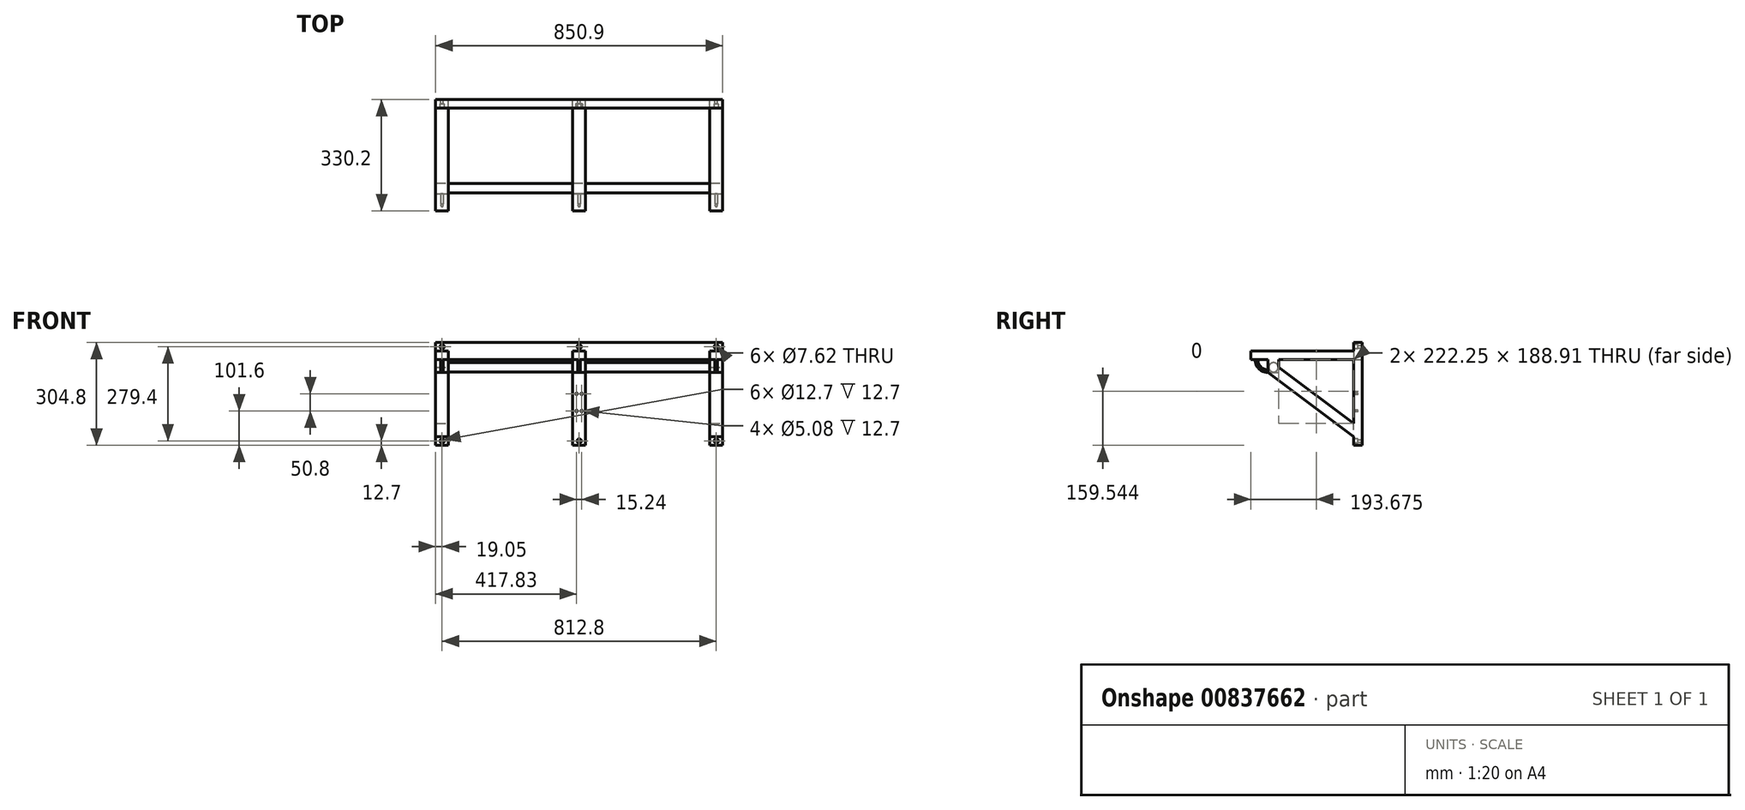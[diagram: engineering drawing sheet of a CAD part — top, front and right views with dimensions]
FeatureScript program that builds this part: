
annotation { "Feature Type Name" : "Feature", "Feature Type Description" : "" }
export const myFeature = defineFeature(function(context is Context, id is Id, definition is map)
    precondition{}
    {
        {
            var Q0;
            Q0=qCreatedBy(makeId("Front.planeOp"),FACE);
            var sketch = newSketch(context, id + "F0", { "sketchPlane" : qUnion([Q0])});
            skLineSegment(sketch, "E0.bottom", {"start": v(19.05, -152.4) * mm, "end": v(-19.05, -152.4) * mm});
            skLineSegment(sketch, "E0.top", {"start": v(19.05, 152.4) * mm, "end": v(-19.05, 152.4) * mm});
            skLineSegment(sketch, "E0.left", {"start": v(19.05, -152.4) * mm, "end": v(19.05, 152.4) * mm});
            skLineSegment(sketch, "E0.right", {"start": v(-19.05, -152.4) * mm, "end": v(-19.05, 152.4) * mm});
            skPoint(sketch, "E0.middle", {"position": v(0, 0) * mm});
            skLineSegment(sketch, "E1.bottom", {"start": v(-387.35, -152.4) * mm, "end": v(-425.45, -152.4) * mm});
            skLineSegment(sketch, "E1.top", {"start": v(-387.35, 152.4) * mm, "end": v(-425.45, 152.4) * mm});
            skLineSegment(sketch, "E1.left", {"start": v(-387.35, -152.4) * mm, "end": v(-387.35, 152.4) * mm});
            skLineSegment(sketch, "E1.right", {"start": v(-425.45, -152.4) * mm, "end": v(-425.45, 152.4) * mm});
            skPoint(sketch, "E1.middle", {"position": v(-406.4, 0) * mm});
            skLineSegment(sketch, "E2.bottom", {"start": v(425.45, -152.4) * mm, "end": v(387.35, -152.4) * mm});
            skLineSegment(sketch, "E2.top", {"start": v(425.45, 152.4) * mm, "end": v(387.35, 152.4) * mm});
            skLineSegment(sketch, "E2.left", {"start": v(425.45, -152.4) * mm, "end": v(425.45, 152.4) * mm});
            skLineSegment(sketch, "E2.right", {"start": v(387.35, -152.4) * mm, "end": v(387.35, 152.4) * mm});
            skPoint(sketch, "E2.middle", {"position": v(406.4, 0) * mm});
            skLineSegment(sketch, "E3.bottom", {"start": v(425.45, 101.6) * mm, "end": v(-425.45, 101.6) * mm});
            skLineSegment(sketch, "E3.top", {"start": v(425.45, 127) * mm, "end": v(-425.45, 127) * mm});
            skLineSegment(sketch, "E3.left", {"start": v(425.45, 101.6) * mm, "end": v(425.45, 127) * mm});
            skLineSegment(sketch, "E3.right", {"start": v(-425.45, 101.6) * mm, "end": v(-425.45, 127) * mm});
            skPoint(sketch, "E3.middle", {"position": v(0, 114.3) * mm});
            skSolve(sketch);
        }
        {
            var Q0;
            Q0=qSketchRegion(id+"F0",true);
            extrude(context, id + "F1", {"entities" : qUnion([Q0]), "depth" : 25.4 * mm, "offsetDistance" : 25.4 * mm});
        }
        {
            var Q0;
            Q0=makeQuery(id+"F1.opExtrude","CAP_FACE",FACE,{"disambiguationData":[OSD([sQuery(id+"F0.wireOp",EDGE,"E0.bottom"),sQuery(id+"F0.wireOp",EDGE,"E0.top"),sQuery(id+"F0.wireOp",EDGE,"E0.left"),sQuery(id+"F0.wireOp",EDGE,"E0.right"),sQuery(id+"F0.wireOp",EDGE,"E1.bottom"),sQuery(id+"F0.wireOp",EDGE,"E1.top"),sQuery(id+"F0.wireOp",EDGE,"E1.left"),sQuery(id+"F0.wireOp",EDGE,"E1.right"),sQuery(id+"F0.wireOp",EDGE,"E2.bottom"),sQuery(id+"F0.wireOp",EDGE,"E2.top"),sQuery(id+"F0.wireOp",EDGE,"E2.left"),sQuery(id+"F0.wireOp",EDGE,"E2.right"),sQuery(id+"F0.wireOp",EDGE,"E3.bottom"),sQuery(id+"F0.wireOp",EDGE,"E3.top"),sQuery(id+"F0.wireOp",EDGE,"E3.left"),sQuery(id+"F0.wireOp",EDGE,"E3.right")])],"isStart":false});
            var sketch = newSketch(context, id + "F2", { "sketchPlane" : qUnion([Q0])});
            skLineSegment(sketch, "E4.bottom", {"start": v(-387.35, 101.6) * mm, "end": v(-425.45, 101.6) * mm});
            skLineSegment(sketch, "E4.top", {"start": v(-387.35, 127) * mm, "end": v(-425.45, 127) * mm});
            skLineSegment(sketch, "E4.left", {"start": v(-387.35, 101.6) * mm, "end": v(-387.35, 127) * mm});
            skLineSegment(sketch, "E4.right", {"start": v(-425.45, 101.6) * mm, "end": v(-425.45, 127) * mm});
            skLineSegment(sketch, "E5.bottom", {"start": v(-19.05, 127) * mm, "end": v(19.05, 127) * mm});
            skLineSegment(sketch, "E5.top", {"start": v(-19.05, 101.6) * mm, "end": v(19.05, 101.6) * mm});
            skLineSegment(sketch, "E5.left", {"start": v(-19.05, 127) * mm, "end": v(-19.05, 101.6) * mm});
            skLineSegment(sketch, "E5.right", {"start": v(19.05, 127) * mm, "end": v(19.05, 101.6) * mm});
            skLineSegment(sketch, "E6.bottom", {"start": v(387.35, 127) * mm, "end": v(425.45, 127) * mm});
            skLineSegment(sketch, "E6.top", {"start": v(387.35, 101.6) * mm, "end": v(425.45, 101.6) * mm});
            skLineSegment(sketch, "E6.left", {"start": v(387.35, 127) * mm, "end": v(387.35, 101.6) * mm});
            skLineSegment(sketch, "E6.right", {"start": v(425.45, 127) * mm, "end": v(425.45, 101.6) * mm});
            skSolve(sketch);
        }
        {
            var Q0;
            Q0=qSketchRegion(id+"F2",true);
            extrude(context, id + "F3", {"entities" : qUnion([Q0]), "operationType" : NewBodyOperationType.ADD, "depth" : 304.8 * mm, "offsetDistance" : 25.4 * mm});
        }
        {
            var Q0;
            {var subQ0=sQuery(id+"F0.wireOp",EDGE,"E1.left");var subQ1=sQuery(id+"F0.wireOp",EDGE,"E1.top");var subQ2=sQuery(id+"F0.wireOp",EDGE,"E3.top");var subQ4=sQuery(id+"F0.wireOp",EDGE,"E3.right");var subQ5=sQuery(id+"F0.wireOp",EDGE,"E1.right");var subQ6=sQuery(id+"F0.wireOp",EDGE,"E0.right");var subQ7=makeQuery(id+"F1.opExtrude","CAP_FACE",FACE,{"disambiguationData":[OSD([sQuery(id+"F0.wireOp",EDGE,"E0.bottom"),sQuery(id+"F0.wireOp",EDGE,"E0.top"),sQuery(id+"F0.wireOp",EDGE,"E0.left"),subQ6,sQuery(id+"F0.wireOp",EDGE,"E1.bottom"),subQ1,subQ0,subQ5,sQuery(id+"F0.wireOp",EDGE,"E2.bottom"),sQuery(id+"F0.wireOp",EDGE,"E2.top"),sQuery(id+"F0.wireOp",EDGE,"E2.left"),sQuery(id+"F0.wireOp",EDGE,"E2.right"),sQuery(id+"F0.wireOp",EDGE,"E3.bottom"),subQ2,sQuery(id+"F0.wireOp",EDGE,"E3.left"),subQ4])],"isStart":false});Q0=makeQuery(id+"F3.boolean.opBoolean","SPLIT",FACE,{"disambiguationData":[TD([subQ7,makeQuery(id+"F1.opExtrude","SWEPT_FACE",FACE,{"disambiguationData":[OSD([subQ1])]}),makeQuery(id+"F1.opExtrude","SWEPT_FACE",FACE,{"disambiguationData":[OSD([subQ0]),TDD([makeQuery(id+"F0.imprint","IMPRINT",EDGE,{"disambiguationData":[TD([[makeQuery(id+"F0.imprint","INTERSECT",VERTEX,{"derivedFrom":[subQ1,subQ0]}),1.0]])],"derivedFrom":subQ0})])]}),makeQuery(id+"F1.opExtrude","SWEPT_FACE",FACE,{"disambiguationData":[OSD([subQ5,subQ4])]}),makeQuery(id+"F1.opExtrude","SWEPT_FACE",FACE,{"disambiguationData":[OSD([subQ2]),TDD([makeQuery(id+"F0.imprint","IMPRINT",EDGE,{"disambiguationData":[TD([[makeQuery(id+"F0.imprint","INTERSECT",VERTEX,{"derivedFrom":[subQ6,subQ2]}),-1.0]])],"derivedFrom":subQ2})])]}),makeQuery(id+"F3.opExtrude","SWEPT_FACE",FACE,{"disambiguationData":[OSD([sQuery(id+"F2.wireOp",EDGE,"E4.top")])]}),makeQuery(id+"F3.opExtrude","SWEPT_FACE",FACE,{"disambiguationData":[OSD([sQuery(id+"F2.wireOp",EDGE,"E4.left")])]}),makeQuery(id+"F3.opExtrude","SWEPT_FACE",FACE,{"disambiguationData":[OSD([sQuery(id+"F2.wireOp",EDGE,"E4.right")])]})])],"derivedFrom":subQ7});}
            var sketch = newSketch(context, id + "F4", { "sketchPlane" : qUnion([Q0])});
            skLineSegment(sketch, "E7.bottom", {"start": v(-425.45, 152.4) * mm, "end": v(425.45, 152.4) * mm});
            skLineSegment(sketch, "E7.top", {"start": v(-425.45, 127) * mm, "end": v(425.45, 127) * mm});
            skLineSegment(sketch, "E7.left", {"start": v(-425.45, 152.4) * mm, "end": v(-425.45, 127) * mm});
            skLineSegment(sketch, "E7.right", {"start": v(425.45, 152.4) * mm, "end": v(425.45, 127) * mm});
            skSolve(sketch);
        }
        {
            var Q0;
            Q0 = qSketchRegion(id + "F4", true);
            extrude(context, id + "F5", {"entities" : qUnion([Q0]), "operationType" : NewBodyOperationType.ADD, "oppositeDirection" : true, "depth" : 25.4 * mm, "offsetDistance" : 25.4 * mm});
        }
        {
            var Q0;
            Q0=makeQuery(id+"F3.boolean.opBoolean","MERGE",FACE,{"derivedFrom":[makeQuery(id+"F1.opExtrude","SWEPT_FACE",FACE,{"disambiguationData":[OSD([sQuery(id+"F0.wireOp",EDGE,"E2.left"),sQuery(id+"F0.wireOp",EDGE,"E3.left")])]}),makeQuery(id+"F3.opExtrude","SWEPT_FACE",FACE,{"disambiguationData":[OSD([sQuery(id+"F2.wireOp",EDGE,"E6.right")])]})]});
            var sketch = newSketch(context, id + "F6", { "sketchPlane" : qUnion([Q0])});
            skLineSegment(sketch, "E8", {"start": v(-25.4, -127) * mm, "end": v(-279.4, 63.5) * mm});
            skLineSegment(sketch, "E9", {"start": v(-279.4, 63.5) * mm, "end": v(-279.4, 101.6) * mm});
            skLineSegment(sketch, "E10", {"start": v(-279.4, 101.6) * mm, "end": v(-247.65, 101.6) * mm});
            skLineSegment(sketch, "E11", {"start": v(-247.65, 101.6) * mm, "end": v(-247.65, 79.38) * mm});
            skLineSegment(sketch, "E12", {"start": v(-247.65, 79.38) * mm, "end": v(-25.4, -87.31) * mm});
            skLineSegment(sketch, "E13", {"start": v(-25.4, -87.31) * mm, "end": v(-25.4, -127) * mm});
            skSolve(sketch);
        }
        {
            var Q0;
            Q0 = qSketchRegion(id + "F6", true);
            extrude(context, id + "F7", {"entities" : qUnion([Q0]), "operationType" : NewBodyOperationType.ADD, "oppositeDirection" : true, "depth" : 38.1 * mm, "offsetDistance" : 25.4 * mm});
        }
        {
            var Q0;
            Q0=makeQuery(id+"F3.opExtrude","SWEPT_FACE",FACE,{"disambiguationData":[OSD([sQuery(id+"F2.wireOp",EDGE,"E4.left")])]});
            var sketch = newSketch(context, id + "F8", { "sketchPlane" : qUnion([Q0])});
            skLineSegment(sketch, "E14", {"start": v(-25.4, -127) * mm, "end": v(-279.4, 63.5) * mm});
            skLineSegment(sketch, "E15", {"start": v(-279.4, 63.5) * mm, "end": v(-279.4, 101.6) * mm});
            skLineSegment(sketch, "E16", {"start": v(-279.4, 101.6) * mm, "end": v(-247.65, 101.6) * mm});
            skLineSegment(sketch, "E17", {"start": v(-247.65, 101.6) * mm, "end": v(-247.65, 79.38) * mm});
            skLineSegment(sketch, "E18", {"start": v(-247.65, 79.38) * mm, "end": v(-25.4, -87.31) * mm});
            skLineSegment(sketch, "E19", {"start": v(-25.4, -87.31) * mm, "end": v(-25.4, -127) * mm});
            skSolve(sketch);
        }
        {
            var Q0;
            Q0 = qSketchRegion(id + "F8", true);
            extrude(context, id + "F9", {"entities" : qUnion([Q0]), "operationType" : NewBodyOperationType.ADD, "oppositeDirection" : true, "depth" : 38.1 * mm, "offsetDistance" : 25.4 * mm});
        }
        {
            var Q0;
            Q0=makeQuery(id+"F3.opExtrude","SWEPT_FACE",FACE,{"disambiguationData":[OSD([sQuery(id+"F2.wireOp",EDGE,"E5.right")])]});
            var sketch = newSketch(context, id + "F10", { "sketchPlane" : qUnion([Q0])});
            skLineSegment(sketch, "E20.bottom", {"start": v(-279.7, 101.6) * mm, "end": v(-247.95, 101.6) * mm});
            skLineSegment(sketch, "E20.top", {"start": v(-279.7, 63.5) * mm, "end": v(-247.95, 63.5) * mm});
            skLineSegment(sketch, "E20.left", {"start": v(-279.7, 101.6) * mm, "end": v(-279.7, 63.5) * mm});
            skLineSegment(sketch, "E20.right", {"start": v(-247.95, 101.6) * mm, "end": v(-247.95, 63.5) * mm});
            skSolve(sketch);
        }
        {
            var Q0;
            Q0 = qSketchRegion(id + "F10", true);
            extrude(context, id + "F11", {"entities" : qUnion([Q0]), "operationType" : NewBodyOperationType.ADD, "oppositeDirection" : true, "depth" : 38.1 * mm, "offsetDistance" : 25.4 * mm});
        }
        {
            var Q0;
            {var subQ0=sQuery(id+"F0.wireOp",EDGE,"E0.right");var subQ1=sQuery(id+"F0.wireOp",EDGE,"E0.bottom");var subQ2=sQuery(id+"F0.wireOp",EDGE,"E3.bottom");var subQ3=makeQuery(id+"F0.imprint","INTERSECT",VERTEX,{"derivedFrom":[subQ0,subQ2]});var subQ4=sQuery(id+"F0.wireOp",EDGE,"E0.left");var subQ5=makeQuery(id+"F0.imprint","INTERSECT",VERTEX,{"derivedFrom":[subQ4,subQ2]});var subQ6=sQuery(id+"F0.wireOp",EDGE,"E2.right");var subQ7=sQuery(id+"F0.wireOp",EDGE,"E1.left");var subQ8=makeQuery(id+"F1.opExtrude","CAP_FACE",FACE,{"disambiguationData":[OSD([subQ1,sQuery(id+"F0.wireOp",EDGE,"E0.top"),subQ4,subQ0,sQuery(id+"F0.wireOp",EDGE,"E1.bottom"),sQuery(id+"F0.wireOp",EDGE,"E1.top"),subQ7,sQuery(id+"F0.wireOp",EDGE,"E1.right"),sQuery(id+"F0.wireOp",EDGE,"E2.bottom"),sQuery(id+"F0.wireOp",EDGE,"E2.top"),sQuery(id+"F0.wireOp",EDGE,"E2.left"),subQ6,subQ2,sQuery(id+"F0.wireOp",EDGE,"E3.top"),sQuery(id+"F0.wireOp",EDGE,"E3.left"),sQuery(id+"F0.wireOp",EDGE,"E3.right")])],"isStart":false});Q0=makeQuery(id+"F3.boolean.opBoolean","SPLIT",FACE,{"disambiguationData":[TD([makeQuery(id+"F1.opExtrude","SWEPT_FACE",FACE,{"disambiguationData":[OSD([subQ1])]}),subQ8,makeQuery(id+"F1.opExtrude","SWEPT_FACE",FACE,{"disambiguationData":[OSD([subQ4]),TDD([makeQuery(id+"F0.imprint","IMPRINT",EDGE,{"disambiguationData":[TD([[makeQuery(id+"F0.imprint","INTERSECT",VERTEX,{"derivedFrom":[subQ1,subQ4]}),-1.0]])],"derivedFrom":subQ4})])]}),makeQuery(id+"F1.opExtrude","SWEPT_FACE",FACE,{"disambiguationData":[OSD([subQ0]),TDD([makeQuery(id+"F0.imprint","IMPRINT",EDGE,{"disambiguationData":[TD([[makeQuery(id+"F0.imprint","INTERSECT",VERTEX,{"derivedFrom":[subQ1,subQ0]}),-1.0]])],"derivedFrom":subQ0})])]}),makeQuery(id+"F1.opExtrude","SWEPT_FACE",FACE,{"disambiguationData":[OSD([subQ2]),TDD([makeQuery(id+"F0.imprint","IMPRINT",EDGE,{"disambiguationData":[TD([[subQ5,1.0]])],"derivedFrom":subQ2})])]}),makeQuery(id+"F1.opExtrude","SWEPT_FACE",FACE,{"disambiguationData":[OSD([subQ2]),TDD([makeQuery(id+"F0.imprint","IMPRINT",EDGE,{"disambiguationData":[TD([[subQ3,-1.0]])],"derivedFrom":subQ2})])]}),makeQuery(id+"F3.opExtrude","SWEPT_FACE",FACE,{"disambiguationData":[OSD([sQuery(id+"F2.wireOp",EDGE,"E5.top")])]}),makeQuery(id+"F3.opExtrude","SWEPT_FACE",FACE,{"disambiguationData":[OSD([sQuery(id+"F2.wireOp",EDGE,"E5.left")])]}),makeQuery(id+"F3.opExtrude","SWEPT_FACE",FACE,{"disambiguationData":[OSD([sQuery(id+"F2.wireOp",EDGE,"E5.right")])]})])],"derivedFrom":subQ8});}
            var sketch = newSketch(context, id + "F12", { "sketchPlane" : qUnion([Q0])});
            skCircle(sketch, "E21", {"center": v(-7.62, 0) * mm, "radius": 2.54 * mm});
            skCircle(sketch, "E22.MirrorC", {"center": v(7.62, 0) * mm, "radius": 2.54 * mm});
            skCircle(sketch, "E23.MirrorC", {"center": v(-7.62, -50.8) * mm, "radius": 2.54 * mm});
            skCircle(sketch, "E24.MirrorC", {"center": v(7.62, -50.8) * mm, "radius": 2.54 * mm});
            skSolve(sketch);
        }
        {
            var Q0;
            Q0 = qSketchRegion(id + "F12", true);
            extrude(context, id + "F13", {"entities" : qUnion([Q0]), "operationType" : NewBodyOperationType.REMOVE, "oppositeDirection" : true, "depth" : 12.7 * mm, "offsetDistance" : 25.4 * mm});
        }
        {
            var Q0;
            Q0=qCreatedBy(makeId("Right.planeOp"),FACE);
            var sketch = newSketch(context, id + "F14", { "sketchPlane" : qUnion([Q0])});
            skCircle(sketch, "E25", {"center": v(-263.27, 78.74) * mm, "radius": 13.97 * mm});
            skSolve(sketch);
        }
        {
            var Q0;
            Q0 = qSketchRegion(id + "F14", true);
            extrude(context, id + "F15", {"entities" : qUnion([Q0]), "operationType" : NewBodyOperationType.ADD, "oppositeDirection" : true, "depth" : 406.4 * mm, "offsetDistance" : 25.4 * mm, "hasSecondDirection" : true, "secondDirectionOppositeDirection" : false, "secondDirectionDepth" : 406.4 * mm});
        }
        {
            var Q0;
            Q0=makeQuery(id+"F9.boolean.opBoolean","MERGE",FACE,{"derivedFrom":[makeQuery(id+"F3.boolean.opBoolean","MERGE",FACE,{"derivedFrom":[makeQuery(id+"F1.opExtrude","SWEPT_FACE",FACE,{"disambiguationData":[OSD([sQuery(id+"F0.wireOp",EDGE,"E1.right"),sQuery(id+"F0.wireOp",EDGE,"E3.right")])]}),makeQuery(id+"F3.opExtrude","SWEPT_FACE",FACE,{"disambiguationData":[OSD([sQuery(id+"F2.wireOp",EDGE,"E4.right")])]})]}),makeQuery(id+"F9.opExtrude","CAP_FACE",FACE,{"disambiguationData":[OSD([sQuery(id+"F8.wireOp",EDGE,"E14"),sQuery(id+"F8.wireOp",EDGE,"E15"),sQuery(id+"F8.wireOp",EDGE,"E16"),sQuery(id+"F8.wireOp",EDGE,"E17"),sQuery(id+"F8.wireOp",EDGE,"E18"),sQuery(id+"F8.wireOp",EDGE,"E19")])],"isStart":false})]});
            var sketch = newSketch(context, id + "F16", { "sketchPlane" : qUnion([Q0])});
            skArc(sketch, "E26", {"start": v(279.4, 63.5) * mm, "mid": v(306.34, 74.66) * mm, "end": v(317.5, 101.6) * mm});
            skArc(sketch, "E27", {"start": v(279.4, 71.12) * mm, "mid": v(300.95, 80.05) * mm, "end": v(309.88, 101.6) * mm});
            skLineSegment(sketch, "E28", {"start": v(309.88, 101.6) * mm, "end": v(317.5, 101.6) * mm});
            skLineSegment(sketch, "E29", {"start": v(279.4, 63.5) * mm, "end": v(279.4, 71.12) * mm});
            skSolve(sketch);
        }
        {
            var Q0;
            Q0 = qSketchRegion(id + "F16", true);
            extrude(context, id + "F17", {"entities" : qUnion([Q0]), "operationType" : NewBodyOperationType.ADD, "oppositeDirection" : true, "depth" : 38.1 * mm, "offsetDistance" : 25.4 * mm});
        }
        {
            var Q0;
            Q0=makeQuery(id+"F11.boolean.opBoolean","MERGE",FACE,{"derivedFrom":[makeQuery(id+"F3.opExtrude","SWEPT_FACE",FACE,{"disambiguationData":[OSD([sQuery(id+"F2.wireOp",EDGE,"E5.left")])]}),makeQuery(id+"F11.opExtrude","CAP_FACE",FACE,{"disambiguationData":[OSD([sQuery(id+"F10.wireOp",EDGE,"E20.bottom"),sQuery(id+"F10.wireOp",EDGE,"E20.top"),sQuery(id+"F10.wireOp",EDGE,"E20.left"),sQuery(id+"F10.wireOp",EDGE,"E20.right")])],"isStart":false})]});
            var sketch = newSketch(context, id + "F18", { "sketchPlane" : qUnion([Q0])});
            skArc(sketch, "E30", {"start": v(279.7, 63.5) * mm, "mid": v(306.64, 74.66) * mm, "end": v(317.8, 101.6) * mm});
            skArc(sketch, "E31", {"start": v(279.7, 71.12) * mm, "mid": v(301.25, 80.05) * mm, "end": v(310.18, 101.6) * mm});
            skLineSegment(sketch, "E32", {"start": v(310.18, 101.6) * mm, "end": v(317.8, 101.6) * mm});
            skLineSegment(sketch, "E33", {"start": v(279.7, 63.5) * mm, "end": v(279.7, 71.12) * mm});
            skSolve(sketch);
        }
        {
            var Q0;
            Q0 = qSketchRegion(id + "F18", true);
            extrude(context, id + "F19", {"entities" : qUnion([Q0]), "operationType" : NewBodyOperationType.ADD, "oppositeDirection" : true, "depth" : 38.1 * mm, "offsetDistance" : 25.4 * mm});
        }
        {
            var Q0;
            {var subQ0=sQuery(id+"F0.wireOp",EDGE,"E2.right");Q0=makeQuery(id+"F7.boolean.opBoolean","MERGE",FACE,{"derivedFrom":[makeQuery(id+"F1.opExtrude","SWEPT_FACE",FACE,{"disambiguationData":[OSD([subQ0]),TDD([makeQuery(id+"F0.imprint","IMPRINT",EDGE,{"disambiguationData":[TD([[makeQuery(id+"F0.imprint","INTERSECT",VERTEX,{"derivedFrom":[sQuery(id+"F0.wireOp",EDGE,"E2.bottom"),subQ0]}),-1.0]])],"derivedFrom":subQ0})])]}),makeQuery(id+"F3.opExtrude","SWEPT_FACE",FACE,{"disambiguationData":[OSD([sQuery(id+"F2.wireOp",EDGE,"E6.left")])]}),makeQuery(id+"F7.opExtrude","CAP_FACE",FACE,{"disambiguationData":[OSD([sQuery(id+"F6.wireOp",EDGE,"E8"),sQuery(id+"F6.wireOp",EDGE,"E9"),sQuery(id+"F6.wireOp",EDGE,"E10"),sQuery(id+"F6.wireOp",EDGE,"E11"),sQuery(id+"F6.wireOp",EDGE,"E12"),sQuery(id+"F6.wireOp",EDGE,"E13")])],"isStart":false})]});}
            var sketch = newSketch(context, id + "F20", { "sketchPlane" : qUnion([Q0])});
            skArc(sketch, "E34", {"start": v(279.4, 63.5) * mm, "mid": v(306.34, 74.66) * mm, "end": v(317.5, 101.6) * mm});
            skArc(sketch, "E35", {"start": v(279.4, 71.12) * mm, "mid": v(300.95, 80.05) * mm, "end": v(309.88, 101.6) * mm});
            skLineSegment(sketch, "E36", {"start": v(309.88, 101.6) * mm, "end": v(317.5, 101.6) * mm});
            skLineSegment(sketch, "E37", {"start": v(279.4, 63.5) * mm, "end": v(279.4, 71.12) * mm});
            skSolve(sketch);
        }
        {
            var Q0;
            Q0 = qSketchRegion(id + "F20", true);
            extrude(context, id + "F21", {"entities" : qUnion([Q0]), "operationType" : NewBodyOperationType.ADD, "oppositeDirection" : true, "depth" : 38.1 * mm, "offsetDistance" : 25.4 * mm});
        }
        {
            var Q0;
            Q0=makeQuery(id+"F3.opExtrude","CAP_FACE",FACE,{"disambiguationData":[OSD([sQuery(id+"F2.wireOp",EDGE,"E4.bottom"),sQuery(id+"F2.wireOp",EDGE,"E4.top"),sQuery(id+"F2.wireOp",EDGE,"E4.left"),sQuery(id+"F2.wireOp",EDGE,"E4.right")])],"isStart":false});
            var sketch = newSketch(context, id + "F22", { "sketchPlane" : qUnion([Q0])});
            skLineSegment(sketch, "E38.bottom", {"start": v(-425.45, 101.6) * mm, "end": v(-410.21, 101.6) * mm});
            skLineSegment(sketch, "E38.top", {"start": v(-425.45, 62.58) * mm, "end": v(-410.21, 62.58) * mm});
            skLineSegment(sketch, "E38.left", {"start": v(-425.45, 101.6) * mm, "end": v(-425.45, 62.58) * mm});
            skLineSegment(sketch, "E38.right", {"start": v(-410.21, 101.6) * mm, "end": v(-410.21, 62.58) * mm});
            skLineSegment(sketch, "E39.bottom", {"start": v(-387.35, 101.6) * mm, "end": v(-402.59, 101.6) * mm});
            skLineSegment(sketch, "E39.top", {"start": v(-387.35, 62.58) * mm, "end": v(-402.59, 62.58) * mm});
            skLineSegment(sketch, "E39.left", {"start": v(-387.35, 101.6) * mm, "end": v(-387.35, 62.58) * mm});
            skLineSegment(sketch, "E39.right", {"start": v(-402.59, 101.6) * mm, "end": v(-402.59, 62.58) * mm});
            skSolve(sketch);
        }
        {
            var Q0;
            Q0 = qSketchRegion(id + "F22", true);
            extrude(context, id + "F23", {"entities" : qUnion([Q0]), "operationType" : NewBodyOperationType.REMOVE, "oppositeDirection" : true, "depth" : 50.8 * mm, "offsetDistance" : 25.4 * mm});
        }
        {
            var Q0;
            Q0=makeQuery(id+"F3.opExtrude","CAP_FACE",FACE,{"disambiguationData":[OSD([sQuery(id+"F2.wireOp",EDGE,"E5.bottom"),sQuery(id+"F2.wireOp",EDGE,"E5.top"),sQuery(id+"F2.wireOp",EDGE,"E5.left"),sQuery(id+"F2.wireOp",EDGE,"E5.right")])],"isStart":false});
            var sketch = newSketch(context, id + "F24", { "sketchPlane" : qUnion([Q0])});
            skLineSegment(sketch, "E40.bottom", {"start": v(-19.05, 101.6) * mm, "end": v(-3.8, 101.6) * mm});
            skLineSegment(sketch, "E40.top", {"start": v(-19.05, 62.58) * mm, "end": v(-3.8, 62.58) * mm});
            skLineSegment(sketch, "E40.left", {"start": v(-19.05, 101.6) * mm, "end": v(-19.05, 62.58) * mm});
            skLineSegment(sketch, "E40.right", {"start": v(-3.8, 101.6) * mm, "end": v(-3.8, 62.58) * mm});
            skLineSegment(sketch, "E41.bottom", {"start": v(19.05, 101.6) * mm, "end": v(3.8, 101.6) * mm});
            skLineSegment(sketch, "E41.top", {"start": v(19.05, 62.58) * mm, "end": v(3.8, 62.58) * mm});
            skLineSegment(sketch, "E41.left", {"start": v(19.05, 101.6) * mm, "end": v(19.05, 62.58) * mm});
            skLineSegment(sketch, "E41.right", {"start": v(3.8, 101.6) * mm, "end": v(3.8, 62.58) * mm});
            skSolve(sketch);
        }
        {
            var Q0;
            Q0 = qSketchRegion(id + "F24", true);
            extrude(context, id + "F25", {"entities" : qUnion([Q0]), "operationType" : NewBodyOperationType.REMOVE, "oppositeDirection" : true, "depth" : 50.8 * mm, "offsetDistance" : 25.4 * mm});
        }
        {
            var Q0;
            Q0=makeQuery(id+"F3.opExtrude","CAP_FACE",FACE,{"disambiguationData":[OSD([sQuery(id+"F2.wireOp",EDGE,"E6.bottom"),sQuery(id+"F2.wireOp",EDGE,"E6.top"),sQuery(id+"F2.wireOp",EDGE,"E6.left"),sQuery(id+"F2.wireOp",EDGE,"E6.right")])],"isStart":false});
            var sketch = newSketch(context, id + "F26", { "sketchPlane" : qUnion([Q0])});
            skLineSegment(sketch, "E42.bottom", {"start": v(387.35, 101.6) * mm, "end": v(402.59, 101.6) * mm});
            skLineSegment(sketch, "E42.top", {"start": v(387.35, 62.58) * mm, "end": v(402.59, 62.58) * mm});
            skLineSegment(sketch, "E42.left", {"start": v(387.35, 101.6) * mm, "end": v(387.35, 62.58) * mm});
            skLineSegment(sketch, "E42.right", {"start": v(402.59, 101.6) * mm, "end": v(402.59, 62.58) * mm});
            skLineSegment(sketch, "E43.bottom", {"start": v(425.45, 101.6) * mm, "end": v(410.21, 101.6) * mm});
            skLineSegment(sketch, "E43.top", {"start": v(425.45, 62.58) * mm, "end": v(410.21, 62.58) * mm});
            skLineSegment(sketch, "E43.left", {"start": v(425.45, 101.6) * mm, "end": v(425.45, 62.58) * mm});
            skLineSegment(sketch, "E43.right", {"start": v(410.21, 101.6) * mm, "end": v(410.21, 62.58) * mm});
            skSolve(sketch);
        }
        {
            var Q0;
            Q0 = qSketchRegion(id + "F26", true);
            extrude(context, id + "F27", {"entities" : qUnion([Q0]), "operationType" : NewBodyOperationType.REMOVE, "oppositeDirection" : true, "depth" : 50.8 * mm, "offsetDistance" : 25.4 * mm});
        }
        {
            var Q0;
            Q0=makeQuery(id+"F27.boolean.opBoolean","INTERSECT",EDGE,{"derivedFrom":[makeQuery(id+"F21.opExtrude","SWEPT_FACE",FACE,{"disambiguationData":[OSD([sQuery(id+"F20.wireOp",EDGE,"E34")])]}),makeQuery(id+"F27.opExtrude","SWEPT_FACE",FACE,{"disambiguationData":[OSD([sQuery(id+"F26.wireOp",EDGE,"E42.right")])]})]});
            var Q1;
            Q1=makeQuery(id+"F27.boolean.opBoolean","INTERSECT",EDGE,{"derivedFrom":[makeQuery(id+"F21.opExtrude","SWEPT_FACE",FACE,{"disambiguationData":[OSD([sQuery(id+"F20.wireOp",EDGE,"E35")])]}),makeQuery(id+"F27.opExtrude","SWEPT_FACE",FACE,{"disambiguationData":[OSD([sQuery(id+"F26.wireOp",EDGE,"E42.right")])]})]});
            var Q2;
            Q2=makeQuery(id+"F27.boolean.opBoolean","INTERSECT",EDGE,{"derivedFrom":[makeQuery(id+"F21.opExtrude","SWEPT_FACE",FACE,{"disambiguationData":[OSD([sQuery(id+"F20.wireOp",EDGE,"E34")])]}),makeQuery(id+"F27.opExtrude","SWEPT_FACE",FACE,{"disambiguationData":[OSD([sQuery(id+"F26.wireOp",EDGE,"E43.right")])]})]});
            var Q3;
            Q3=makeQuery(id+"F27.boolean.opBoolean","INTERSECT",EDGE,{"derivedFrom":[makeQuery(id+"F21.opExtrude","SWEPT_FACE",FACE,{"disambiguationData":[OSD([sQuery(id+"F20.wireOp",EDGE,"E35")])]}),makeQuery(id+"F27.opExtrude","SWEPT_FACE",FACE,{"disambiguationData":[OSD([sQuery(id+"F26.wireOp",EDGE,"E43.right")])]})]});
            var Q4;
            Q4=makeQuery(id+"F25.boolean.opBoolean","INTERSECT",EDGE,{"derivedFrom":[makeQuery(id+"F19.opExtrude","SWEPT_FACE",FACE,{"disambiguationData":[OSD([sQuery(id+"F18.wireOp",EDGE,"E31")])]}),makeQuery(id+"F25.opExtrude","SWEPT_FACE",FACE,{"disambiguationData":[OSD([sQuery(id+"F24.wireOp",EDGE,"E41.right")])]})]});
            var Q5;
            Q5=makeQuery(id+"F25.boolean.opBoolean","INTERSECT",EDGE,{"derivedFrom":[makeQuery(id+"F19.opExtrude","SWEPT_FACE",FACE,{"disambiguationData":[OSD([sQuery(id+"F18.wireOp",EDGE,"E30")])]}),makeQuery(id+"F25.opExtrude","SWEPT_FACE",FACE,{"disambiguationData":[OSD([sQuery(id+"F24.wireOp",EDGE,"E41.right")])]})]});
            var Q6;
            Q6=makeQuery(id+"F25.boolean.opBoolean","INTERSECT",EDGE,{"derivedFrom":[makeQuery(id+"F19.opExtrude","SWEPT_FACE",FACE,{"disambiguationData":[OSD([sQuery(id+"F18.wireOp",EDGE,"E31")])]}),makeQuery(id+"F25.opExtrude","SWEPT_FACE",FACE,{"disambiguationData":[OSD([sQuery(id+"F24.wireOp",EDGE,"E40.right")])]})]});
            var Q7;
            Q7=makeQuery(id+"F25.boolean.opBoolean","INTERSECT",EDGE,{"derivedFrom":[makeQuery(id+"F19.opExtrude","SWEPT_FACE",FACE,{"disambiguationData":[OSD([sQuery(id+"F18.wireOp",EDGE,"E30")])]}),makeQuery(id+"F25.opExtrude","SWEPT_FACE",FACE,{"disambiguationData":[OSD([sQuery(id+"F24.wireOp",EDGE,"E40.right")])]})]});
            var Q8;
            Q8=makeQuery(id+"F23.boolean.opBoolean","INTERSECT",EDGE,{"derivedFrom":[makeQuery(id+"F17.opExtrude","SWEPT_FACE",FACE,{"disambiguationData":[OSD([sQuery(id+"F16.wireOp",EDGE,"E27")])]}),makeQuery(id+"F23.opExtrude","SWEPT_FACE",FACE,{"disambiguationData":[OSD([sQuery(id+"F22.wireOp",EDGE,"E38.right")])]})]});
            var Q9;
            Q9=makeQuery(id+"F23.boolean.opBoolean","INTERSECT",EDGE,{"derivedFrom":[makeQuery(id+"F17.opExtrude","SWEPT_FACE",FACE,{"disambiguationData":[OSD([sQuery(id+"F16.wireOp",EDGE,"E26")])]}),makeQuery(id+"F23.opExtrude","SWEPT_FACE",FACE,{"disambiguationData":[OSD([sQuery(id+"F22.wireOp",EDGE,"E38.right")])]})]});
            var Q10;
            Q10=makeQuery(id+"F23.boolean.opBoolean","INTERSECT",EDGE,{"derivedFrom":[makeQuery(id+"F17.opExtrude","SWEPT_FACE",FACE,{"disambiguationData":[OSD([sQuery(id+"F16.wireOp",EDGE,"E27")])]}),makeQuery(id+"F23.opExtrude","SWEPT_FACE",FACE,{"disambiguationData":[OSD([sQuery(id+"F22.wireOp",EDGE,"E39.right")])]})]});
            var Q11;
            Q11=makeQuery(id+"F23.boolean.opBoolean","INTERSECT",EDGE,{"derivedFrom":[makeQuery(id+"F17.opExtrude","SWEPT_FACE",FACE,{"disambiguationData":[OSD([sQuery(id+"F16.wireOp",EDGE,"E26")])]}),makeQuery(id+"F23.opExtrude","SWEPT_FACE",FACE,{"disambiguationData":[OSD([sQuery(id+"F22.wireOp",EDGE,"E39.right")])]})]});
            fillet(context, id + "F28", {"entities" : qUnion([Q0, Q1, Q2, Q3, Q4, Q5, Q6, Q7, Q8, Q9, Q10, Q11]), "radius" : 3.8 * mm, "tangentPropagation" : true, "allowEdgeOverflow" : false});
        }
        {
            var Q0;
            Q0=makeQuery(id+"F5.boolean.opBoolean","MERGE",FACE,{"derivedFrom":[makeQuery(id+"F1.opExtrude","CAP_FACE",FACE,{"disambiguationData":[OSD([sQuery(id+"F0.wireOp",EDGE,"E0.bottom"),sQuery(id+"F0.wireOp",EDGE,"E0.top"),sQuery(id+"F0.wireOp",EDGE,"E0.left"),sQuery(id+"F0.wireOp",EDGE,"E0.right"),sQuery(id+"F0.wireOp",EDGE,"E1.bottom"),sQuery(id+"F0.wireOp",EDGE,"E1.top"),sQuery(id+"F0.wireOp",EDGE,"E1.left"),sQuery(id+"F0.wireOp",EDGE,"E1.right"),sQuery(id+"F0.wireOp",EDGE,"E2.bottom"),sQuery(id+"F0.wireOp",EDGE,"E2.top"),sQuery(id+"F0.wireOp",EDGE,"E2.left"),sQuery(id+"F0.wireOp",EDGE,"E2.right"),sQuery(id+"F0.wireOp",EDGE,"E3.bottom"),sQuery(id+"F0.wireOp",EDGE,"E3.top"),sQuery(id+"F0.wireOp",EDGE,"E3.left"),sQuery(id+"F0.wireOp",EDGE,"E3.right")])],"isStart":true}),makeQuery(id+"F5.opExtrude","CAP_FACE",FACE,{"disambiguationData":[OSD([sQuery(id+"F4.wireOp",EDGE,"E7.bottom"),sQuery(id+"F4.wireOp",EDGE,"E7.top"),sQuery(id+"F4.wireOp",EDGE,"E7.left"),sQuery(id+"F4.wireOp",EDGE,"E7.right")])],"isStart":false})]});
            var sketch = newSketch(context, id + "F29", { "sketchPlane" : qUnion([Q0])});
            skCircle(sketch, "E44", {"center": v(0, -139.7) * mm, "radius": 3.81 * mm});
            skPoint(sketch, "E44.centerSnap0", {"position": v(0, -152.4) * mm});
            skCircle(sketch, "E45", {"center": v(0, 139.7) * mm, "radius": 3.81 * mm});
            skCircle(sketch, "E46", {"center": v(-406.4, 139.7) * mm, "radius": 3.81 * mm});
            skPoint(sketch, "E46.centerSnap0", {"position": v(-406.4, -152.4) * mm});
            skCircle(sketch, "E47", {"center": v(-406.4, -139.7) * mm, "radius": 3.81 * mm});
            skCircle(sketch, "E48", {"center": v(406.4, -139.7) * mm, "radius": 3.81 * mm});
            skPoint(sketch, "E48.centerSnap0", {"position": v(406.4, -152.4) * mm});
            skCircle(sketch, "E49", {"center": v(406.4, 139.7) * mm, "radius": 3.81 * mm});
            skSolve(sketch);
        }
        {
            var Q0;
            Q0 = qSketchRegion(id + "F29", true);
            extrude(context, id + "F30", {"entities" : qUnion([Q0]), "operationType" : NewBodyOperationType.REMOVE, "oppositeDirection" : true, "depth" : 25.4 * mm, "offsetDistance" : 25.4 * mm});
        }
        {
            var Q0;
            {var subQ0=sQuery(id+"F0.wireOp",EDGE,"E3.left");var subQ1=sQuery(id+"F0.wireOp",EDGE,"E2.left");var subQ2=sQuery(id+"F0.wireOp",EDGE,"E2.top");var subQ3=sQuery(id+"F0.wireOp",EDGE,"E2.right");var subQ4=sQuery(id+"F0.wireOp",EDGE,"E3.top");var subQ6=makeQuery(id+"F1.opExtrude","SWEPT_FACE",FACE,{"disambiguationData":[OSD([subQ3]),TDD([makeQuery(id+"F0.imprint","IMPRINT",EDGE,{"disambiguationData":[TD([[makeQuery(id+"F0.imprint","INTERSECT",VERTEX,{"derivedFrom":[subQ2,subQ3]}),1.0]])],"derivedFrom":subQ3})])]});var subQ7=makeQuery(id+"F3.opExtrude","SWEPT_FACE",FACE,{"disambiguationData":[OSD([sQuery(id+"F2.wireOp",EDGE,"E6.left")])]});var subQ8=sQuery(id+"F0.wireOp",EDGE,"E3.right");var subQ9=sQuery(id+"F0.wireOp",EDGE,"E3.bottom");var subQ10=sQuery(id+"F0.wireOp",EDGE,"E2.bottom");var subQ11=sQuery(id+"F0.wireOp",EDGE,"E1.right");var subQ12=sQuery(id+"F0.wireOp",EDGE,"E1.left");var subQ13=sQuery(id+"F0.wireOp",EDGE,"E1.top");var subQ14=sQuery(id+"F0.wireOp",EDGE,"E1.bottom");var subQ15=sQuery(id+"F0.wireOp",EDGE,"E0.right");var subQ16=sQuery(id+"F0.wireOp",EDGE,"E0.left");var subQ17=sQuery(id+"F0.wireOp",EDGE,"E0.top");var subQ18=sQuery(id+"F0.wireOp",EDGE,"E0.bottom");var subQ19=makeQuery(id+"F1.opExtrude","CAP_FACE",FACE,{"disambiguationData":[OSD([subQ18,subQ17,subQ16,subQ15,subQ14,subQ13,subQ12,subQ11,subQ10,subQ2,subQ1,subQ3,subQ9,subQ4,subQ0,subQ8])],"isStart":false});var subQ20=makeQuery(id+"F3.opExtrude","SWEPT_FACE",FACE,{"disambiguationData":[OSD([sQuery(id+"F2.wireOp",EDGE,"E6.bottom")])]});var subQ21=makeQuery(id+"F0.imprint","INTERSECT",VERTEX,{"derivedFrom":[subQ16,subQ4]});var subQ22=makeQuery(id+"F1.opExtrude","SWEPT_FACE",FACE,{"disambiguationData":[OSD([subQ4]),TDD([makeQuery(id+"F0.imprint","IMPRINT",EDGE,{"disambiguationData":[TD([[subQ21,1.0]])],"derivedFrom":subQ4})])]});var subQ24=makeQuery(id+"F1.opExtrude","SWEPT_FACE",FACE,{"disambiguationData":[OSD([subQ12]),TDD([makeQuery(id+"F0.imprint","IMPRINT",EDGE,{"disambiguationData":[TD([[makeQuery(id+"F0.imprint","INTERSECT",VERTEX,{"derivedFrom":[subQ13,subQ12]}),1.0]])],"derivedFrom":subQ12})])]});var subQ25=makeQuery(id+"F0.imprint","INTERSECT",VERTEX,{"derivedFrom":[subQ15,subQ4]});var subQ26=makeQuery(id+"F1.opExtrude","SWEPT_FACE",FACE,{"disambiguationData":[OSD([subQ4]),TDD([makeQuery(id+"F0.imprint","IMPRINT",EDGE,{"disambiguationData":[TD([[subQ25,-1.0]])],"derivedFrom":subQ4})])]});var subQ27=makeQuery(id+"F3.opExtrude","SWEPT_FACE",FACE,{"disambiguationData":[OSD([sQuery(id+"F2.wireOp",EDGE,"E4.top")])]});var subQ28=makeQuery(id+"F3.opExtrude","SWEPT_FACE",FACE,{"disambiguationData":[OSD([sQuery(id+"F2.wireOp",EDGE,"E4.left")])]});var subQ29=makeQuery(id+"F1.opExtrude","SWEPT_FACE",FACE,{"disambiguationData":[OSD([subQ15]),TDD([makeQuery(id+"F0.imprint","IMPRINT",EDGE,{"disambiguationData":[TD([[makeQuery(id+"F0.imprint","INTERSECT",VERTEX,{"derivedFrom":[subQ17,subQ15]}),1.0]])],"derivedFrom":subQ15})])]});var subQ30=makeQuery(id+"F0.imprint","INTERSECT",VERTEX,{"derivedFrom":[subQ15,subQ9]});var subQ32=makeQuery(id+"F3.opExtrude","SWEPT_FACE",FACE,{"disambiguationData":[OSD([sQuery(id+"F2.wireOp",EDGE,"E5.bottom")])]});var subQ33=makeQuery(id+"F3.opExtrude","SWEPT_FACE",FACE,{"disambiguationData":[OSD([sQuery(id+"F2.wireOp",EDGE,"E5.top")])]});var subQ34=makeQuery(id+"F3.opExtrude","SWEPT_FACE",FACE,{"disambiguationData":[OSD([sQuery(id+"F2.wireOp",EDGE,"E5.left")])]});var subQ35=makeQuery(id+"F3.opExtrude","SWEPT_FACE",FACE,{"disambiguationData":[OSD([sQuery(id+"F2.wireOp",EDGE,"E5.right")])]});var subQ36=makeQuery(id+"F0.imprint","INTERSECT",VERTEX,{"derivedFrom":[subQ16,subQ9]});var subQ38=makeQuery(id+"F1.opExtrude","SWEPT_FACE",FACE,{"disambiguationData":[OSD([subQ16]),TDD([makeQuery(id+"F0.imprint","IMPRINT",EDGE,{"disambiguationData":[TD([[makeQuery(id+"F0.imprint","INTERSECT",VERTEX,{"derivedFrom":[subQ17,subQ16]}),1.0]])],"derivedFrom":subQ16})])]});Q0=makeQuery(id+"F5.boolean.opBoolean","MERGE",FACE,{"derivedFrom":[makeQuery(id+"F3.boolean.opBoolean","SPLIT",FACE,{"disambiguationData":[TD([subQ19,makeQuery(id+"F1.opExtrude","SWEPT_FACE",FACE,{"disambiguationData":[OSD([subQ17])]}),subQ38,subQ29,subQ22,subQ26,subQ32,subQ34,subQ35])],"derivedFrom":subQ19}),makeQuery(id+"F3.boolean.opBoolean","SPLIT",FACE,{"disambiguationData":[TD([subQ19,makeQuery(id+"F1.opExtrude","SWEPT_FACE",FACE,{"disambiguationData":[OSD([subQ16]),TDD([makeQuery(id+"F0.imprint","IMPRINT",EDGE,{"disambiguationData":[TD([[makeQuery(id+"F0.imprint","INTERSECT",VERTEX,{"derivedFrom":[subQ18,subQ16]}),-1.0]])],"derivedFrom":subQ16})])]}),subQ38,makeQuery(id+"F1.opExtrude","SWEPT_FACE",FACE,{"disambiguationData":[OSD([subQ3]),TDD([makeQuery(id+"F0.imprint","IMPRINT",EDGE,{"disambiguationData":[TD([[makeQuery(id+"F0.imprint","INTERSECT",VERTEX,{"derivedFrom":[subQ10,subQ3]}),-1.0]])],"derivedFrom":subQ3})])]}),subQ6,makeQuery(id+"F1.opExtrude","SWEPT_FACE",FACE,{"disambiguationData":[OSD([subQ9]),TDD([makeQuery(id+"F0.imprint","IMPRINT",EDGE,{"disambiguationData":[TD([[subQ36,1.0]])],"derivedFrom":subQ9})])]}),subQ22,subQ32,subQ33,subQ35,subQ20,makeQuery(id+"F3.opExtrude","SWEPT_FACE",FACE,{"disambiguationData":[OSD([sQuery(id+"F2.wireOp",EDGE,"E6.top")])]}),subQ7])],"derivedFrom":subQ19}),makeQuery(id+"F3.boolean.opBoolean","SPLIT",FACE,{"disambiguationData":[TD([subQ19,makeQuery(id+"F1.opExtrude","SWEPT_FACE",FACE,{"disambiguationData":[OSD([subQ15]),TDD([makeQuery(id+"F0.imprint","IMPRINT",EDGE,{"disambiguationData":[TD([[makeQuery(id+"F0.imprint","INTERSECT",VERTEX,{"derivedFrom":[subQ18,subQ15]}),-1.0]])],"derivedFrom":subQ15})])]}),subQ29,makeQuery(id+"F1.opExtrude","SWEPT_FACE",FACE,{"disambiguationData":[OSD([subQ12]),TDD([makeQuery(id+"F0.imprint","IMPRINT",EDGE,{"disambiguationData":[TD([[makeQuery(id+"F0.imprint","INTERSECT",VERTEX,{"derivedFrom":[subQ14,subQ12]}),-1.0]])],"derivedFrom":subQ12})])]}),subQ24,makeQuery(id+"F1.opExtrude","SWEPT_FACE",FACE,{"disambiguationData":[OSD([subQ9]),TDD([makeQuery(id+"F0.imprint","IMPRINT",EDGE,{"disambiguationData":[TD([[subQ30,-1.0]])],"derivedFrom":subQ9})])]}),subQ26,makeQuery(id+"F3.opExtrude","SWEPT_FACE",FACE,{"disambiguationData":[OSD([sQuery(id+"F2.wireOp",EDGE,"E4.bottom")])]}),subQ27,subQ28,subQ32,subQ33,subQ34])],"derivedFrom":subQ19}),makeQuery(id+"F3.boolean.opBoolean","SPLIT",FACE,{"disambiguationData":[TD([subQ19,makeQuery(id+"F1.opExtrude","SWEPT_FACE",FACE,{"disambiguationData":[OSD([subQ13])]}),subQ24,makeQuery(id+"F1.opExtrude","SWEPT_FACE",FACE,{"disambiguationData":[OSD([subQ11,subQ8])]}),subQ26,subQ27,subQ28,makeQuery(id+"F3.opExtrude","SWEPT_FACE",FACE,{"disambiguationData":[OSD([sQuery(id+"F2.wireOp",EDGE,"E4.right")])]})])],"derivedFrom":subQ19}),makeQuery(id+"F3.boolean.opBoolean","SPLIT",FACE,{"disambiguationData":[TD([subQ19,makeQuery(id+"F1.opExtrude","SWEPT_FACE",FACE,{"disambiguationData":[OSD([subQ2])]}),makeQuery(id+"F1.opExtrude","SWEPT_FACE",FACE,{"disambiguationData":[OSD([subQ1,subQ0])]}),subQ6,subQ22,subQ20,subQ7,makeQuery(id+"F3.opExtrude","SWEPT_FACE",FACE,{"disambiguationData":[OSD([sQuery(id+"F2.wireOp",EDGE,"E6.right")])]})])],"derivedFrom":subQ19}),makeQuery(id+"F5.opExtrude","CAP_FACE",FACE,{"disambiguationData":[OSD([sQuery(id+"F4.wireOp",EDGE,"E7.bottom"),sQuery(id+"F4.wireOp",EDGE,"E7.top"),sQuery(id+"F4.wireOp",EDGE,"E7.left"),sQuery(id+"F4.wireOp",EDGE,"E7.right")])],"isStart":true})]});}
            var sketch = newSketch(context, id + "F31", { "sketchPlane" : qUnion([Q0])});
            skCircle(sketch, "E50", {"center": v(-406.4, 139.7) * mm, "radius": 6.35 * mm});
            skCircle(sketch, "E51", {"center": v(0, 139.7) * mm, "radius": 6.35 * mm});
            skCircle(sketch, "E52", {"center": v(406.4, 139.7) * mm, "radius": 6.35 * mm});
            skSolve(sketch);
        }
        {
            var Q0;
            Q0 = qSketchRegion(id + "F31", true);
            extrude(context, id + "F32", {"entities" : qUnion([Q0]), "operationType" : NewBodyOperationType.REMOVE, "oppositeDirection" : true, "depth" : 12.7 * mm, "offsetDistance" : 25.4 * mm});
        }
        {
            var Q0;
            {var subQ0=makeQuery(id+"F3.opExtrude","SWEPT_FACE",FACE,{"disambiguationData":[OSD([sQuery(id+"F2.wireOp",EDGE,"E4.left")])]});var subQ2=sQuery(id+"F0.wireOp",EDGE,"E3.right");var subQ3=sQuery(id+"F0.wireOp",EDGE,"E1.right");var subQ4=makeQuery(id+"F1.opExtrude","SWEPT_FACE",FACE,{"disambiguationData":[OSD([subQ3,subQ2])]});var subQ5=sQuery(id+"F0.wireOp",EDGE,"E1.left");var subQ6=sQuery(id+"F0.wireOp",EDGE,"E1.bottom");var subQ7=sQuery(id+"F0.wireOp",EDGE,"E3.bottom");var subQ9=makeQuery(id+"F1.opExtrude","SWEPT_FACE",FACE,{"disambiguationData":[OSD([subQ5]),TDD([makeQuery(id+"F0.imprint","IMPRINT",EDGE,{"disambiguationData":[TD([[makeQuery(id+"F0.imprint","INTERSECT",VERTEX,{"derivedFrom":[subQ6,subQ5]}),-1.0]])],"derivedFrom":subQ5})])]});var subQ10=makeQuery(id+"F1.opExtrude","SWEPT_FACE",FACE,{"disambiguationData":[OSD([subQ6])]});var subQ11=makeQuery(id+"F3.opExtrude","SWEPT_FACE",FACE,{"disambiguationData":[OSD([sQuery(id+"F2.wireOp",EDGE,"E4.right")])]});var subQ17=sQuery(id+"F0.wireOp",EDGE,"E0.right");var subQ18=makeQuery(id+"F1.opExtrude","CAP_FACE",FACE,{"disambiguationData":[OSD([sQuery(id+"F0.wireOp",EDGE,"E0.bottom"),sQuery(id+"F0.wireOp",EDGE,"E0.top"),sQuery(id+"F0.wireOp",EDGE,"E0.left"),subQ17,subQ6,sQuery(id+"F0.wireOp",EDGE,"E1.top"),subQ5,subQ3,sQuery(id+"F0.wireOp",EDGE,"E2.bottom"),sQuery(id+"F0.wireOp",EDGE,"E2.top"),sQuery(id+"F0.wireOp",EDGE,"E2.left"),sQuery(id+"F0.wireOp",EDGE,"E2.right"),subQ7,sQuery(id+"F0.wireOp",EDGE,"E3.top"),sQuery(id+"F0.wireOp",EDGE,"E3.left"),subQ2])],"isStart":false});Q0=makeQuery(id+"F9.boolean.opBoolean","SPLIT",FACE,{"disambiguationData":[TD([subQ10])],"derivedFrom":makeQuery(id+"F3.boolean.opBoolean","SPLIT",FACE,{"disambiguationData":[TD([subQ18,subQ10,subQ9,subQ4,makeQuery(id+"F1.opExtrude","SWEPT_FACE",FACE,{"disambiguationData":[OSD([subQ7]),TDD([makeQuery(id+"F0.imprint","IMPRINT",EDGE,{"disambiguationData":[TD([[makeQuery(id+"F0.imprint","INTERSECT",VERTEX,{"derivedFrom":[subQ17,subQ7]}),-1.0]])],"derivedFrom":subQ7})])]}),makeQuery(id+"F3.opExtrude","SWEPT_FACE",FACE,{"disambiguationData":[OSD([sQuery(id+"F2.wireOp",EDGE,"E4.bottom")])]}),subQ0,subQ11])],"derivedFrom":subQ18})});}
            var sketch = newSketch(context, id + "F33", { "sketchPlane" : qUnion([Q0])});
            skCircle(sketch, "E53", {"center": v(-406.4, -139.7) * mm, "radius": 6.35 * mm});
            skSolve(sketch);
        }
        {
            var Q0;
            Q0 = qSketchRegion(id + "F33", true);
            extrude(context, id + "F34", {"entities" : qUnion([Q0]), "operationType" : NewBodyOperationType.REMOVE, "oppositeDirection" : true, "depth" : 12.7 * mm, "offsetDistance" : 25.4 * mm});
        }
        {
            var Q0;
            {var subQ0=sQuery(id+"F0.wireOp",EDGE,"E0.right");var subQ1=sQuery(id+"F0.wireOp",EDGE,"E0.bottom");var subQ2=sQuery(id+"F0.wireOp",EDGE,"E3.bottom");var subQ3=makeQuery(id+"F0.imprint","INTERSECT",VERTEX,{"derivedFrom":[subQ0,subQ2]});var subQ4=sQuery(id+"F0.wireOp",EDGE,"E0.left");var subQ5=makeQuery(id+"F0.imprint","INTERSECT",VERTEX,{"derivedFrom":[subQ4,subQ2]});var subQ6=sQuery(id+"F0.wireOp",EDGE,"E2.right");var subQ7=sQuery(id+"F0.wireOp",EDGE,"E1.left");var subQ8=makeQuery(id+"F1.opExtrude","CAP_FACE",FACE,{"disambiguationData":[OSD([subQ1,sQuery(id+"F0.wireOp",EDGE,"E0.top"),subQ4,subQ0,sQuery(id+"F0.wireOp",EDGE,"E1.bottom"),sQuery(id+"F0.wireOp",EDGE,"E1.top"),subQ7,sQuery(id+"F0.wireOp",EDGE,"E1.right"),sQuery(id+"F0.wireOp",EDGE,"E2.bottom"),sQuery(id+"F0.wireOp",EDGE,"E2.top"),sQuery(id+"F0.wireOp",EDGE,"E2.left"),subQ6,subQ2,sQuery(id+"F0.wireOp",EDGE,"E3.top"),sQuery(id+"F0.wireOp",EDGE,"E3.left"),sQuery(id+"F0.wireOp",EDGE,"E3.right")])],"isStart":false});Q0=makeQuery(id+"F3.boolean.opBoolean","SPLIT",FACE,{"disambiguationData":[TD([makeQuery(id+"F1.opExtrude","SWEPT_FACE",FACE,{"disambiguationData":[OSD([subQ1])]}),subQ8,makeQuery(id+"F1.opExtrude","SWEPT_FACE",FACE,{"disambiguationData":[OSD([subQ4]),TDD([makeQuery(id+"F0.imprint","IMPRINT",EDGE,{"disambiguationData":[TD([[makeQuery(id+"F0.imprint","INTERSECT",VERTEX,{"derivedFrom":[subQ1,subQ4]}),-1.0]])],"derivedFrom":subQ4})])]}),makeQuery(id+"F1.opExtrude","SWEPT_FACE",FACE,{"disambiguationData":[OSD([subQ0]),TDD([makeQuery(id+"F0.imprint","IMPRINT",EDGE,{"disambiguationData":[TD([[makeQuery(id+"F0.imprint","INTERSECT",VERTEX,{"derivedFrom":[subQ1,subQ0]}),-1.0]])],"derivedFrom":subQ0})])]}),makeQuery(id+"F1.opExtrude","SWEPT_FACE",FACE,{"disambiguationData":[OSD([subQ2]),TDD([makeQuery(id+"F0.imprint","IMPRINT",EDGE,{"disambiguationData":[TD([[subQ5,1.0]])],"derivedFrom":subQ2})])]}),makeQuery(id+"F1.opExtrude","SWEPT_FACE",FACE,{"disambiguationData":[OSD([subQ2]),TDD([makeQuery(id+"F0.imprint","IMPRINT",EDGE,{"disambiguationData":[TD([[subQ3,-1.0]])],"derivedFrom":subQ2})])]}),makeQuery(id+"F3.opExtrude","SWEPT_FACE",FACE,{"disambiguationData":[OSD([sQuery(id+"F2.wireOp",EDGE,"E5.top")])]}),makeQuery(id+"F3.opExtrude","SWEPT_FACE",FACE,{"disambiguationData":[OSD([sQuery(id+"F2.wireOp",EDGE,"E5.left")])]}),makeQuery(id+"F3.opExtrude","SWEPT_FACE",FACE,{"disambiguationData":[OSD([sQuery(id+"F2.wireOp",EDGE,"E5.right")])]})])],"derivedFrom":subQ8});}
            var sketch = newSketch(context, id + "F35", { "sketchPlane" : qUnion([Q0])});
            skCircle(sketch, "E54", {"center": v(0, -139.7) * mm, "radius": 6.35 * mm});
            skSolve(sketch);
        }
        {
            var Q0;
            Q0 = qSketchRegion(id + "F35", true);
            extrude(context, id + "F36", {"entities" : qUnion([Q0]), "operationType" : NewBodyOperationType.REMOVE, "oppositeDirection" : true, "depth" : 12.7 * mm, "offsetDistance" : 25.4 * mm});
        }
        {
            var Q0;
            {var subQ0=makeQuery(id+"F3.opExtrude","SWEPT_FACE",FACE,{"disambiguationData":[OSD([sQuery(id+"F2.wireOp",EDGE,"E6.left")])]});var subQ1=sQuery(id+"F0.wireOp",EDGE,"E2.right");var subQ2=sQuery(id+"F0.wireOp",EDGE,"E2.bottom");var subQ3=sQuery(id+"F0.wireOp",EDGE,"E3.bottom");var subQ5=makeQuery(id+"F1.opExtrude","SWEPT_FACE",FACE,{"disambiguationData":[OSD([subQ1]),TDD([makeQuery(id+"F0.imprint","IMPRINT",EDGE,{"disambiguationData":[TD([[makeQuery(id+"F0.imprint","INTERSECT",VERTEX,{"derivedFrom":[subQ2,subQ1]}),-1.0]])],"derivedFrom":subQ1})])]});var subQ6=sQuery(id+"F0.wireOp",EDGE,"E3.left");var subQ7=sQuery(id+"F0.wireOp",EDGE,"E2.left");var subQ8=makeQuery(id+"F1.opExtrude","SWEPT_FACE",FACE,{"disambiguationData":[OSD([subQ7,subQ6])]});var subQ9=makeQuery(id+"F1.opExtrude","SWEPT_FACE",FACE,{"disambiguationData":[OSD([subQ2])]});var subQ16=makeQuery(id+"F3.opExtrude","SWEPT_FACE",FACE,{"disambiguationData":[OSD([sQuery(id+"F2.wireOp",EDGE,"E6.right")])]});var subQ17=sQuery(id+"F0.wireOp",EDGE,"E0.left");var subQ18=makeQuery(id+"F1.opExtrude","CAP_FACE",FACE,{"disambiguationData":[OSD([sQuery(id+"F0.wireOp",EDGE,"E0.bottom"),sQuery(id+"F0.wireOp",EDGE,"E0.top"),subQ17,sQuery(id+"F0.wireOp",EDGE,"E0.right"),sQuery(id+"F0.wireOp",EDGE,"E1.bottom"),sQuery(id+"F0.wireOp",EDGE,"E1.top"),sQuery(id+"F0.wireOp",EDGE,"E1.left"),sQuery(id+"F0.wireOp",EDGE,"E1.right"),subQ2,sQuery(id+"F0.wireOp",EDGE,"E2.top"),subQ7,subQ1,subQ3,sQuery(id+"F0.wireOp",EDGE,"E3.top"),subQ6,sQuery(id+"F0.wireOp",EDGE,"E3.right")])],"isStart":false});Q0=makeQuery(id+"F7.boolean.opBoolean","SPLIT",FACE,{"disambiguationData":[TD([subQ9])],"derivedFrom":makeQuery(id+"F3.boolean.opBoolean","SPLIT",FACE,{"disambiguationData":[TD([subQ18,subQ9,subQ8,subQ5,makeQuery(id+"F1.opExtrude","SWEPT_FACE",FACE,{"disambiguationData":[OSD([subQ3]),TDD([makeQuery(id+"F0.imprint","IMPRINT",EDGE,{"disambiguationData":[TD([[makeQuery(id+"F0.imprint","INTERSECT",VERTEX,{"derivedFrom":[subQ17,subQ3]}),1.0]])],"derivedFrom":subQ3})])]}),makeQuery(id+"F3.opExtrude","SWEPT_FACE",FACE,{"disambiguationData":[OSD([sQuery(id+"F2.wireOp",EDGE,"E6.top")])]}),subQ0,subQ16])],"derivedFrom":subQ18})});}
            var sketch = newSketch(context, id + "F37", { "sketchPlane" : qUnion([Q0])});
            skCircle(sketch, "E55", {"center": v(406.4, -139.7) * mm, "radius": 6.35 * mm});
            skSolve(sketch);
        }
        {
            var Q0;
            Q0 = qSketchRegion(id + "F37", true);
            extrude(context, id + "F38", {"entities" : qUnion([Q0]), "operationType" : NewBodyOperationType.REMOVE, "oppositeDirection" : true, "depth" : 12.7 * mm, "offsetDistance" : 25.4 * mm});
        }
    });
